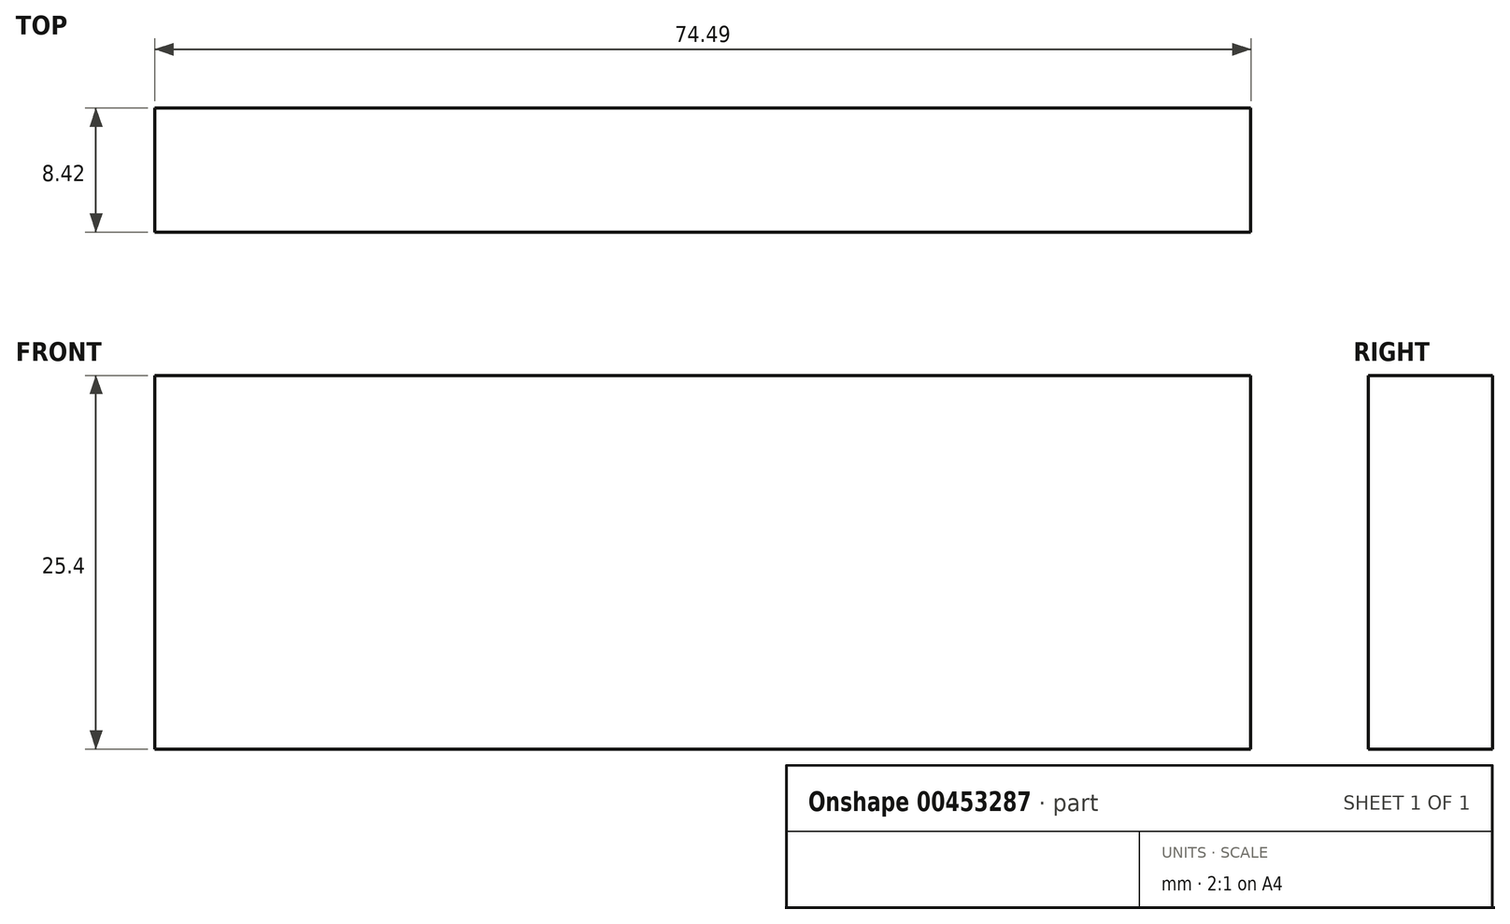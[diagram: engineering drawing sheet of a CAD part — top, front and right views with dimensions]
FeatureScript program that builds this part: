
annotation { "Feature Type Name" : "Feature", "Feature Type Description" : "" }
export const myFeature = defineFeature(function(context is Context, id is Id, definition is map)
    precondition{}
    {
        {
            var Q0;
            Q0=qCreatedBy(makeId("Top.planeOp"),FACE);
            var sketch = newSketch(context, id + "F0", { "sketchPlane" : qUnion([Q0])});
            skLineSegment(sketch, "E0", {"start": v(0, 0) * mm, "end": v(74.49, 0) * mm});
            skLineSegment(sketch, "E1", {"start": v(74.49, 0) * mm, "end": v(74.49, 8.42) * mm});
            skLineSegment(sketch, "E2", {"start": v(74.49, 8.42) * mm, "end": v(0, 8.42) * mm});
            skLineSegment(sketch, "E3", {"start": v(0, 8.42) * mm, "end": v(0, 0) * mm});
            skSolve(sketch);
        }
        {
            var Q0;
            Q0=sQuery(id+"F0.wireOp",EDGE,"E2");
            var Q1;
            Q1=sQuery(id+"F0.wireOp",EDGE,"E3");
            var Q2;
            Q2=sQuery(id+"F0.wireOp",EDGE,"E0");
            var Q3;
            Q3=sQuery(id+"F0.wireOp",EDGE,"E1");
            extrude(context, id + "F1", {"bodyType" : ToolBodyType.SURFACE, "surfaceEntities" : qUnion([Q0, Q1, Q2, Q3]), "depth" : 25.4 * mm});
        }
    });
